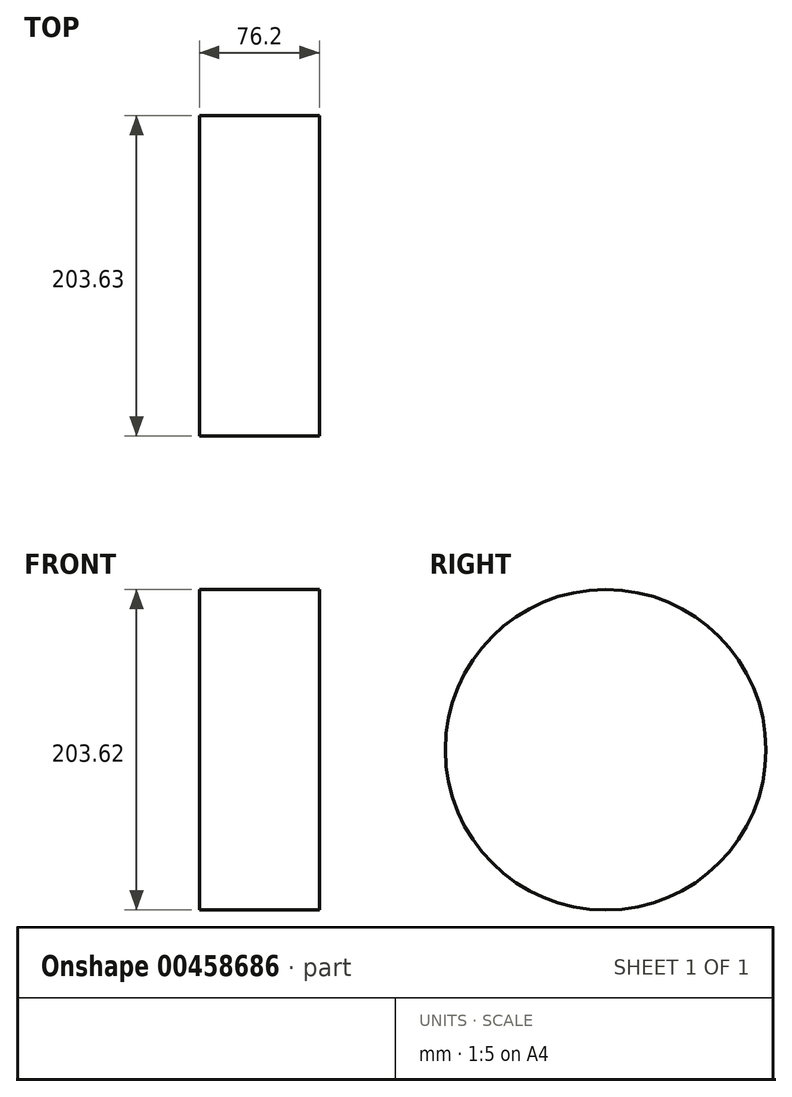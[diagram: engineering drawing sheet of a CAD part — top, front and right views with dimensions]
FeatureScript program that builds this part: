
annotation { "Feature Type Name" : "Feature", "Feature Type Description" : "" }
export const myFeature = defineFeature(function(context is Context, id is Id, definition is map)
    precondition{}
    {
        {
            var Q0;
            Q0=qCreatedBy(makeId("Right.planeOp"),FACE);
            var sketch = newSketch(context, id + "F0", { "sketchPlane" : qUnion([Q0])});
            skCircle(sketch, "E0", {"center": v(-3.89, 0) * mm, "radius": 101.81 * mm});
            skSolve(sketch);
        }
        {
            var Q0;
            Q0=makeQuery(id+"F0.imprint","IMPRINT",FACE,{"disambiguationData":[TD([[makeQuery(id+"F0.imprint","IMPRINT",EDGE,{"derivedFrom":sQuery(id+"F0.wireOp",EDGE,"E0")}),1.0]])]});
            extrude(context, id + "F1", {"entities" : qUnion([Q0]), "depth" : 76.2 * mm});
        }
    });
